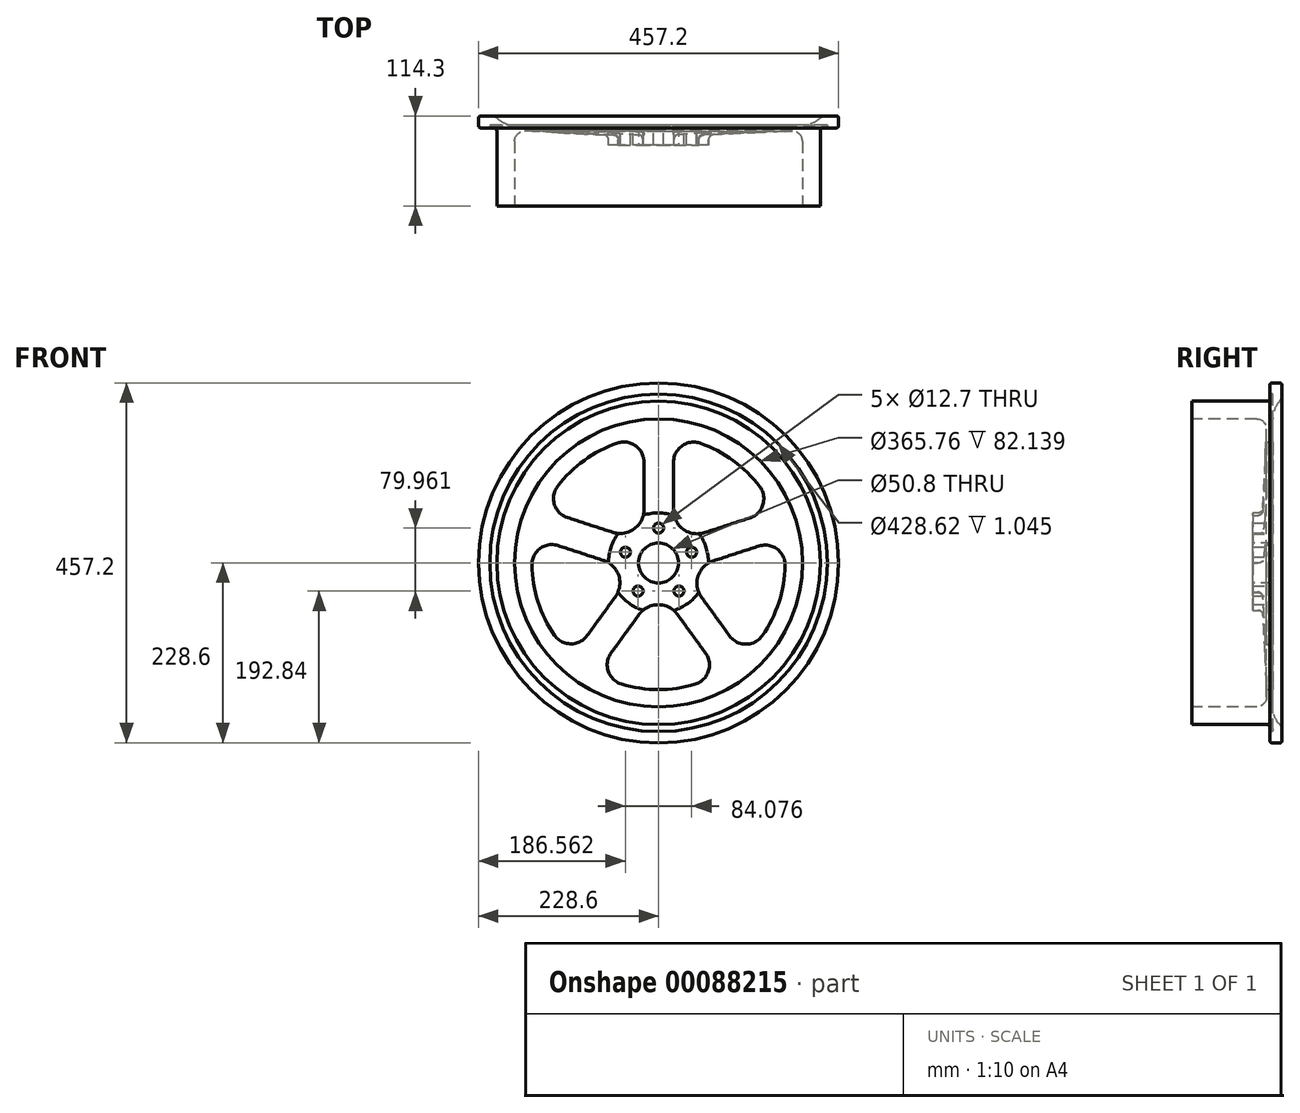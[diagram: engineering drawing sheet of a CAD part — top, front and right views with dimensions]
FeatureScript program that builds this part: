
annotation { "Feature Type Name" : "Feature", "Feature Type Description" : "" }
export const myFeature = defineFeature(function(context is Context, id is Id, definition is map)
    precondition{}
    {
        {
            var Q0;
            Q0=qCreatedBy(makeId("Top.planeOp"),FACE);
            var sketch = newSketch(context, id + "F0", { "sketchPlane" : qUnion([Q0])});
            skLineSegment(sketch, "E0.bottom", {"start": v(-25.4, 0) * mm, "end": v(-63.5, 0) * mm});
            skLineSegment(sketch, "E0.top", {"start": v(-25.4, 25.4) * mm, "end": v(-63.5, 25.4) * mm});
            skLineSegment(sketch, "E0.left", {"start": v(-25.4, 0) * mm, "end": v(-25.4, 25.4) * mm});
            skLineSegment(sketch, "E0.right", {"start": v(-63.5, 0) * mm, "end": v(-63.5, 6.64) * mm});
            skPoint(sketch, "E1.endSnap0", {"position": v(-25.4, 12.7) * mm});
            skLineSegment(sketch, "E2", {"start": v(-25.4, 25.4) * mm, "end": v(-182.88, 25.4) * mm});
            skLineSegment(sketch, "E3", {"start": v(-69.56, 12.98) * mm, "end": v(-169.6, 17.58) * mm});
            skArc(sketch, "E4", {"start": v(-205.46, 18.2) * mm, "mid": v(-207.57, 23.29) * mm, "end": v(-212.67, 25.4) * mm});
            skArc(sketch, "E5", {"start": v(-182.88, 25.4) * mm, "mid": v(-195, 27.69) * mm, "end": v(-205.46, 34.23) * mm});
            skArc(sketch, "E6", {"start": v(-205.46, 34.23) * mm, "mid": v(-208.8, 36.32) * mm, "end": v(-212.67, 37.05) * mm});
            skLineSegment(sketch, "E7", {"start": v(-212.67, 37.05) * mm, "end": v(-214.31, 37.05) * mm});
            skLineSegment(sketch, "E8", {"start": v(-212.67, 25.4) * mm, "end": v(-214.31, 25.4) * mm});
            skLineSegment(sketch, "E9.bottom", {"start": v(-214.31, 37.05) * mm, "end": v(-226.06, 37.05) * mm});
            skLineSegment(sketch, "E9.top", {"start": v(-216.85, 21.81) * mm, "end": v(-226.06, 21.81) * mm});
            skLineSegment(sketch, "E9.left", {"start": v(-214.31, 25.4) * mm, "end": v(-214.31, 24.35) * mm});
            skLineSegment(sketch, "E9.right", {"start": v(-228.6, 34.51) * mm, "end": v(-228.6, 24.35) * mm});
            skPoint(sketch, "E10.visualSharp", {"position": v(-228.6, 37.05) * mm});
            skArc(sketch, "E10.filletArc", {"start": v(-226.06, 37.05) * mm, "mid": v(-227.86, 36.31) * mm, "end": v(-228.6, 34.51) * mm});
            skPoint(sketch, "E11.visualSharp", {"position": v(-228.6, 21.81) * mm});
            skArc(sketch, "E11.filletArc", {"start": v(-228.6, 24.35) * mm, "mid": v(-227.86, 22.56) * mm, "end": v(-226.06, 21.81) * mm});
            skPoint(sketch, "E12.visualSharp", {"position": v(-214.31, 21.81) * mm});
            skArc(sketch, "E12.filletArc", {"start": v(-216.85, 21.81) * mm, "mid": v(-215.05, 22.56) * mm, "end": v(-214.31, 24.35) * mm});
            skLineSegment(sketch, "E13", {"start": v(-234.55, -77.25) * mm, "end": v(-167, -77.25) * mm});
            skLineSegment(sketch, "E14", {"start": v(-205.46, 18.2) * mm, "end": v(-205.46, -77.25) * mm});
            skArc(sketch, "E15.MirrorCS", {"start": v(-228.6, -178.85) * mm, "mid": v(-227.86, -177.05) * mm, "end": v(-226.06, -176.3) * mm});
            skArc(sketch, "E16.MirrorCS", {"start": v(-226.06, -191.55) * mm, "mid": v(-227.86, -190.8) * mm, "end": v(-228.6, -189) * mm});
            skLineSegment(sketch, "E17.MirrorCS", {"start": v(-214.31, -179.9) * mm, "end": v(-214.31, -178.85) * mm});
            skArc(sketch, "E18.MirrorCS", {"start": v(-216.85, -176.3) * mm, "mid": v(-215.05, -177.05) * mm, "end": v(-214.31, -178.85) * mm});
            skLineSegment(sketch, "E19.MirrorCS", {"start": v(-212.67, -179.9) * mm, "end": v(-214.31, -179.9) * mm});
            skLineSegment(sketch, "E20.MirrorCS", {"start": v(-228.6, -189) * mm, "end": v(-228.6, -178.85) * mm});
            skLineSegment(sketch, "E21.MirrorCS", {"start": v(-214.31, -191.55) * mm, "end": v(-226.06, -191.55) * mm});
            skPoint(sketch, "E22.MirrorP", {"position": v(-214.31, -176.3) * mm});
            skArc(sketch, "E23.MirrorCS", {"start": v(-205.46, -188.72) * mm, "mid": v(-208.8, -190.81) * mm, "end": v(-212.67, -191.55) * mm});
            skLineSegment(sketch, "E24.MirrorCS", {"start": v(-212.67, -191.55) * mm, "end": v(-214.31, -191.55) * mm});
            skPoint(sketch, "E25.MirrorP", {"position": v(-228.6, -191.55) * mm});
            skLineSegment(sketch, "E26.MirrorCS", {"start": v(-216.85, -176.3) * mm, "end": v(-226.06, -176.3) * mm});
            skLineSegment(sketch, "E27.MirrorCS", {"start": v(-205.46, -172.68) * mm, "end": v(-205.46, -77.25) * mm});
            skPoint(sketch, "E28.MirrorP", {"position": v(-228.6, -176.3) * mm});
            skArc(sketch, "E29.MirrorCS", {"start": v(-205.46, -172.68) * mm, "mid": v(-207.57, -177.78) * mm, "end": v(-212.67, -179.9) * mm});
            skLineSegment(sketch, "E30", {"start": v(-182.88, 4.9) * mm, "end": v(-182.88, -77.25) * mm});
            skLineSegment(sketch, "E31", {"start": v(-182.88, -77.25) * mm, "end": v(-182.88, -177.44) * mm});
            skPoint(sketch, "E32.visualSharp", {"position": v(-182.88, 18.2) * mm});
            skArc(sketch, "E32.filletArc", {"start": v(-169.6, 17.58) * mm, "mid": v(-178.95, 14.08) * mm, "end": v(-182.88, 4.9) * mm});
            skArc(sketch, "E33.MirrorCS", {"start": v(-185.24, -179.97) * mm, "mid": v(-196.1, -182.63) * mm, "end": v(-205.46, -188.72) * mm});
            skPoint(sketch, "E34.visualSharp", {"position": v(-182.88, -179.9) * mm});
            skArc(sketch, "E34.filletArc", {"start": v(-185.24, -179.97) * mm, "mid": v(-183.56, -179.17) * mm, "end": v(-182.88, -177.44) * mm});
            skPoint(sketch, "E35.visualSharp", {"position": v(-63.5, 12.7) * mm});
            skArc(sketch, "E35.filletArc", {"start": v(-63.5, 6.64) * mm, "mid": v(-65.26, 11.02) * mm, "end": v(-69.56, 12.98) * mm});
            skLineSegment(sketch, "E36", {"start": v(0, 0) * mm, "end": v(0, 64.23) * mm});
            skSolve(sketch);
        }
        {
            var Q0;
            Q0=makeQuery(id+"F0.imprint","IMPRINT",FACE,{"disambiguationData":[TD([[makeQuery(id+"F0.imprint","IMPRINT",EDGE,{"derivedFrom":sQuery(id+"F0.wireOp",EDGE,"E0.bottom")}),-1.0]])]});
            var Q1;
            Q1=makeQuery(id+"F0.imprint","IMPRINT",FACE,{"disambiguationData":[TD([[makeQuery(id+"F0.imprint","IMPRINT",EDGE,{"derivedFrom":sQuery(id+"F0.wireOp",EDGE,"E15.MirrorCS")}),-1.0]])]});
            var Q2;
            Q2=sQuery(id+"F0.wireOp",EDGE,"E36");
            revolve(context, id + "F1", {"entities" : qUnion([Q0, Q1]), "axis" : qUnion([Q2]), "revolveType" : RevolveType.FULL});
        }
        {
            var Q0;
            Q0=makeQuery(id+"F1.opRevolve","SWEPT_FACE",FACE,{"disambiguationData":[OSD([sQuery(id+"F0.wireOp",EDGE,"E2")])]});
            var sketch = newSketch(context, id + "F2", { "sketchPlane" : qUnion([Q0])});
            skPoint(sketch, "E37.center", {"position": v(-0.5, 0) * mm});
            skCircle(sketch, "E38", {"center": v(0, 44.2) * mm, "radius": 6.35 * mm});
            skCircle(sketch, "E39.1.0", {"center": v(-42.04, 13.66) * mm, "radius": 6.35 * mm});
            skCircle(sketch, "E39.2.0", {"center": v(-25.98, -35.76) * mm, "radius": 6.35 * mm});
            skPoint(sketch, "E39.center", {"position": v(0, 0) * mm});
            skCircle(sketch, "E40.1.3.0", {"center": v(25.98, -35.76) * mm, "radius": 6.35 * mm});
            skCircle(sketch, "E41.1.4.0", {"center": v(42.04, 13.66) * mm, "radius": 6.35 * mm});
            skLineSegment(sketch, "E42.0", {"start": v(18.54, 67.38) * mm, "end": v(18.54, 128.2) * mm});
            skLineSegment(sketch, "E43.0", {"start": v(57.85, 38.83) * mm, "end": v(115.87, 57.68) * mm});
            skArc(sketch, "E44", {"start": v(52.18, 152.23) * mm, "mid": v(94.33, 130.38) * mm, "end": v(128.27, 97.18) * mm});
            skArc(sketch, "E45.filletArc", {"start": v(18.54, 67.38) * mm, "mid": v(30.92, 43.1) * mm, "end": v(57.85, 38.83) * mm});
            skArc(sketch, "E46.filletArc", {"start": v(52.18, 152.23) * mm, "mid": v(29.18, 148.87) * mm, "end": v(18.54, 128.2) * mm});
            skArc(sketch, "E47.filletArc", {"start": v(115.87, 57.68) * mm, "mid": v(132.26, 74.23) * mm, "end": v(128.27, 97.18) * mm});
            skLineSegment(sketch, "E48.1.0", {"start": v(-58.36, 38.46) * mm, "end": v(-116.2, 57.25) * mm});
            skArc(sketch, "E48.1.1", {"start": v(-128.66, 96.66) * mm, "mid": v(-132.57, 73.75) * mm, "end": v(-116.2, 57.25) * mm});
            skArc(sketch, "E48.1.2", {"start": v(-58.36, 38.46) * mm, "mid": v(-31.43, 42.72) * mm, "end": v(-19.05, 67.01) * mm});
            skLineSegment(sketch, "E48.1.3", {"start": v(-19.05, 67.01) * mm, "end": v(-19.05, 128.03) * mm});
            skArc(sketch, "E48.1.4", {"start": v(-19.05, 128.03) * mm, "mid": v(-29.73, 148.73) * mm, "end": v(-52.78, 152.02) * mm});
            skArc(sketch, "E48.1.5", {"start": v(-128.66, 96.66) * mm, "mid": v(-94.85, 130) * mm, "end": v(-52.78, 152.02) * mm});
            skLineSegment(sketch, "E48.2.0", {"start": v(-54.6, -43.62) * mm, "end": v(-90.36, -92.82) * mm});
            skArc(sketch, "E48.2.1", {"start": v(-131.7, -92.49) * mm, "mid": v(-111.1, -103.3) * mm, "end": v(-90.36, -92.82) * mm});
            skArc(sketch, "E48.2.2", {"start": v(-54.6, -43.62) * mm, "mid": v(-50.34, -16.69) * mm, "end": v(-69.62, 2.6) * mm});
            skLineSegment(sketch, "E48.2.3", {"start": v(-69.62, 2.6) * mm, "end": v(-127.65, 21.45) * mm});
            skArc(sketch, "E48.2.4", {"start": v(-127.65, 21.45) * mm, "mid": v(-150.63, 17.69) * mm, "end": v(-160.9, -3.22) * mm});
            skArc(sketch, "E48.2.5", {"start": v(-131.7, -92.49) * mm, "mid": v(-152.95, -50.03) * mm, "end": v(-160.9, -3.22) * mm});
            skLineSegment(sketch, "E48.3.0", {"start": v(24.6, -65.41) * mm, "end": v(60.36, -114.62) * mm});
            skArc(sketch, "E48.3.1", {"start": v(47.27, -153.83) * mm, "mid": v(63.9, -137.59) * mm, "end": v(60.36, -114.62) * mm});
            skArc(sketch, "E48.3.2", {"start": v(24.6, -65.41) * mm, "mid": v(0.31, -53.04) * mm, "end": v(-23.98, -65.41) * mm});
            skLineSegment(sketch, "E48.3.3", {"start": v(-23.98, -65.41) * mm, "end": v(-59.84, -114.77) * mm});
            skArc(sketch, "E48.3.4", {"start": v(-59.84, -114.77) * mm, "mid": v(-63.37, -137.8) * mm, "end": v(-46.66, -154.01) * mm});
            skArc(sketch, "E48.3.5", {"start": v(47.27, -153.83) * mm, "mid": v(0.32, -160.92) * mm, "end": v(-46.66, -154.01) * mm});
            skLineSegment(sketch, "E48.4.0", {"start": v(69.82, 3.19) * mm, "end": v(127.66, 21.98) * mm});
            skArc(sketch, "E48.4.1", {"start": v(160.9, -2.58) * mm, "mid": v(150.6, 18.26) * mm, "end": v(127.66, 21.98) * mm});
            skArc(sketch, "E48.4.2", {"start": v(69.82, 3.19) * mm, "mid": v(50.54, -16.09) * mm, "end": v(54.8, -43.02) * mm});
            skLineSegment(sketch, "E48.4.3", {"start": v(54.8, -43.02) * mm, "end": v(90.66, -92.38) * mm});
            skArc(sketch, "E48.4.4", {"start": v(90.66, -92.38) * mm, "mid": v(111.47, -102.85) * mm, "end": v(132.06, -91.97) * mm});
            skArc(sketch, "E48.4.5", {"start": v(160.9, -2.58) * mm, "mid": v(153.15, -49.42) * mm, "end": v(132.06, -91.97) * mm});
            skSolve(sketch);
        }
        {
            var Q0;
            Q0=makeQuery(id+"F2.imprint","IMPRINT",FACE,{"disambiguationData":[TD([[makeQuery(id+"F2.imprint","IMPRINT",EDGE,{"derivedFrom":sQuery(id+"F2.wireOp",EDGE,"E38")}),1.0]])]});
            var Q1;
            Q1=makeQuery(id+"F2.imprint","IMPRINT",FACE,{"disambiguationData":[TD([[makeQuery(id+"F2.imprint","IMPRINT",EDGE,{"derivedFrom":sQuery(id+"F2.wireOp",EDGE,"E41.1.4.0")}),1.0]])]});
            var Q2;
            Q2=makeQuery(id+"F2.imprint","IMPRINT",FACE,{"disambiguationData":[TD([[makeQuery(id+"F2.imprint","IMPRINT",EDGE,{"derivedFrom":sQuery(id+"F2.wireOp",EDGE,"E40.1.3.0")}),1.0]])]});
            var Q3;
            Q3=makeQuery(id+"F2.imprint","IMPRINT",FACE,{"disambiguationData":[TD([[makeQuery(id+"F2.imprint","IMPRINT",EDGE,{"derivedFrom":sQuery(id+"F2.wireOp",EDGE,"E39.2.0")}),1.0]])]});
            var Q4;
            Q4=makeQuery(id+"F2.imprint","IMPRINT",FACE,{"disambiguationData":[TD([[makeQuery(id+"F2.imprint","IMPRINT",EDGE,{"derivedFrom":sQuery(id+"F2.wireOp",EDGE,"E39.1.0")}),1.0]])]});
            var Q5;
            Q5=makeQuery(id+"F2.imprint","IMPRINT",FACE,{"disambiguationData":[TD([[makeQuery(id+"F2.imprint","IMPRINT",EDGE,{"derivedFrom":sQuery(id+"F2.wireOp",EDGE,"E48.1.0")}),-1.0]])]});
            var Q6;
            Q6=makeQuery(id+"F2.imprint","IMPRINT",FACE,{"disambiguationData":[TD([[makeQuery(id+"F2.imprint","IMPRINT",EDGE,{"derivedFrom":sQuery(id+"F2.wireOp",EDGE,"E42.0")}),-1.0]])]});
            var Q7;
            Q7=makeQuery(id+"F2.imprint","IMPRINT",FACE,{"disambiguationData":[TD([[makeQuery(id+"F2.imprint","IMPRINT",EDGE,{"derivedFrom":sQuery(id+"F2.wireOp",EDGE,"E48.4.0")}),-1.0]])]});
            var Q8;
            Q8=makeQuery(id+"F2.imprint","IMPRINT",FACE,{"disambiguationData":[TD([[makeQuery(id+"F2.imprint","IMPRINT",EDGE,{"derivedFrom":sQuery(id+"F2.wireOp",EDGE,"E48.3.0")}),-1.0]])]});
            var Q9;
            Q9=makeQuery(id+"F2.imprint","IMPRINT",FACE,{"disambiguationData":[TD([[makeQuery(id+"F2.imprint","IMPRINT",EDGE,{"derivedFrom":sQuery(id+"F2.wireOp",EDGE,"E48.2.0")}),-1.0]])]});
            extrude(context, id + "F3", {"entities" : qUnion([Q0, Q1, Q2, Q3, Q4, Q5, Q6, Q7, Q8, Q9]), "operationType" : NewBodyOperationType.REMOVE, "endBound" : BoundingType.THROUGH_ALL, "oppositeDirection" : true, "depth" : 25.4 * mm});
        }
    });
